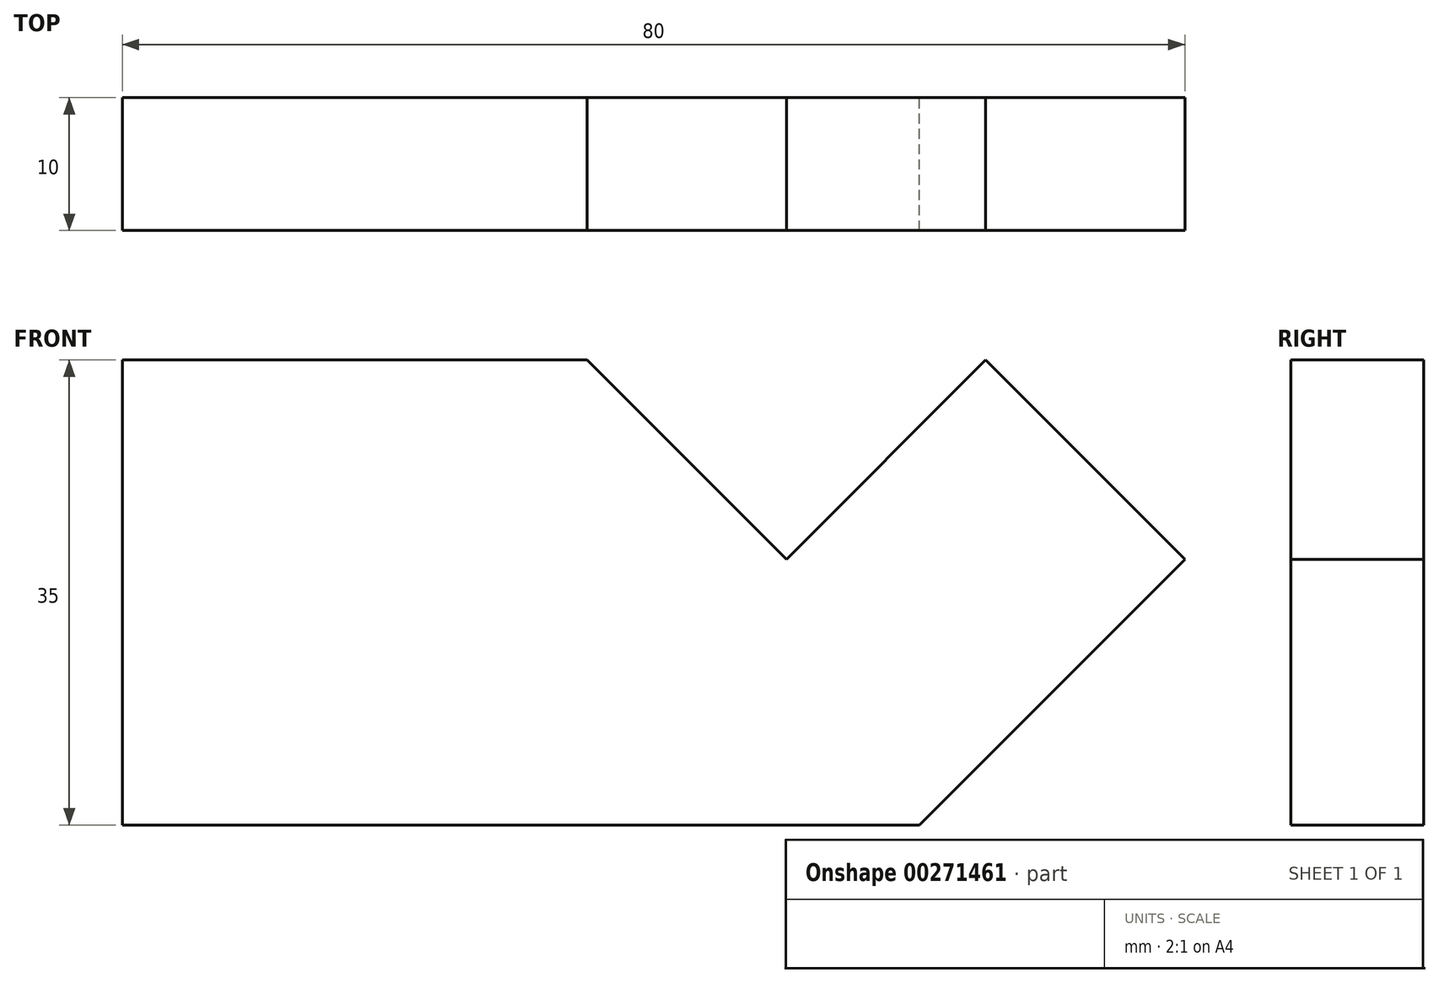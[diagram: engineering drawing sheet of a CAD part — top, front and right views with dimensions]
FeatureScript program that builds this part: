
annotation { "Feature Type Name" : "Feature", "Feature Type Description" : "" }
export const myFeature = defineFeature(function(context is Context, id is Id, definition is map)
    precondition{}
    {
        {
            var Q0;
            Q0=qCreatedBy(makeId("Front.planeOp"),FACE);
            var sketch = newSketch(context, id + "F0", { "sketchPlane" : qUnion([Q0])});
            skLineSegment(sketch, "E0", {"start": v(0, 0) * mm, "end": v(0, 35) * mm});
            skLineSegment(sketch, "E1", {"start": v(0, 35) * mm, "end": v(35, 35) * mm});
            skLineSegment(sketch, "E2", {"start": v(35, 35) * mm, "end": v(50, 20) * mm});
            skLineSegment(sketch, "E3", {"start": v(50, 20) * mm, "end": v(65, 35) * mm});
            skLineSegment(sketch, "E4", {"start": v(65, 35) * mm, "end": v(80, 20) * mm});
            skLineSegment(sketch, "E5", {"start": v(0, 0) * mm, "end": v(60, 0) * mm});
            skLineSegment(sketch, "E6", {"start": v(60, 0) * mm, "end": v(80, 20) * mm});
            skSolve(sketch);
        }
        {
            var Q0;
            Q0=makeQuery(id+"F0.imprint","IMPRINT",FACE,{"disambiguationData":[TD([[makeQuery(id+"F0.imprint","IMPRINT",EDGE,{"derivedFrom":sQuery(id+"F0.wireOp",EDGE,"E0")}),-1.0]])]});
            extrude(context, id + "F1", {"entities" : qUnion([Q0]), "depth" : 10 * mm});
        }
    });
